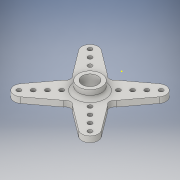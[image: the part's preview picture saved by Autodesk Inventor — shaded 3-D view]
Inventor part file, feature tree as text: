
AUTODESK INVENTOR PART (.ipt)
format: ipt  version: 2016 (Build 200138000, 138)  size: 216,064 bytes
history: native  units: in
note: dims shown in document units (in); Inventor stores cm internally (conversion verified against a paired STEP export)
features: sketch x2, pattern_circular x1, fillet x1, extrude x1
ambient origin geometry x8: Origin, YZ Plane, XZ Plane, XY Plane, X Axis, Y Axis, Z Axis, Center Point
bodies: Solid1 (feature_tree)
feature tree (5):
  pattern_circular  "CirPattern1"
  fillet  "Fillet1"  Radius=0.05in
  sketch  "Sketch1"  dims[d1=0.172in d2=0.0in]
  extrude  "Extrusion1"  [1 undecoded]
  sketch  "Sketch2"
note: 1 required parameter value undecoded (feature->parameter linkage not recoverable at this tier; creation-order binding heuristic only, values carry confidence <= 0.55)
